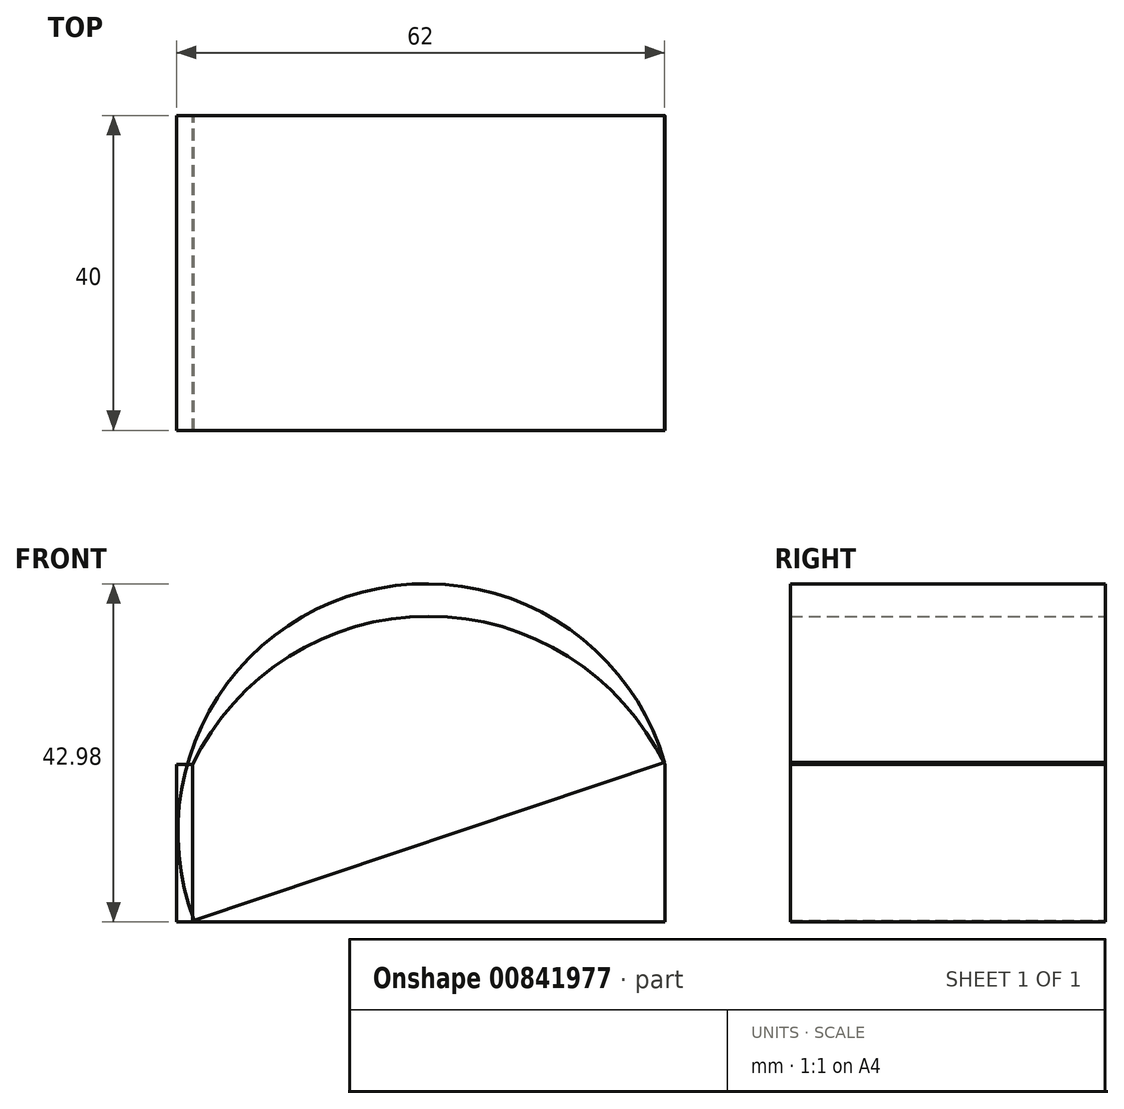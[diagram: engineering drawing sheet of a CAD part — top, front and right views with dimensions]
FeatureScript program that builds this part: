
annotation { "Feature Type Name" : "Feature", "Feature Type Description" : "" }
export const myFeature = defineFeature(function(context is Context, id is Id, definition is map)
    precondition{}
    {
        {
            var Q0;
            Q0=qCreatedBy(makeId("Front.planeOp"),FACE);
            var sketch = newSketch(context, id + "F0", { "sketchPlane" : qUnion([Q0])});
            skLineSegment(sketch, "E0.bottom", {"start": v(-32.74, -13.82) * mm, "end": v(27.26, -13.82) * mm});
            skLineSegment(sketch, "E0.top", {"start": v(-32.74, -33.82) * mm, "end": v(27.26, -33.82) * mm});
            skLineSegment(sketch, "E0.left", {"start": v(-32.74, -13.82) * mm, "end": v(-32.74, -33.82) * mm});
            skLineSegment(sketch, "E0.right", {"start": v(27.26, -13.82) * mm, "end": v(27.26, -33.82) * mm});
            skArc(sketch, "E1", {"start": v(27.26, -13.82) * mm, "mid": v(-2.74, 5.03) * mm, "end": v(-32.74, -13.82) * mm});
            skSolve(sketch);
        }
        {
            var Q0;
            Q0=makeQuery(id+"F0.imprint","IMPRINT",FACE,{"disambiguationData":[TD([[makeQuery(id+"F0.imprint","IMPRINT",EDGE,{"derivedFrom":sQuery(id+"F0.wireOp",EDGE,"E0.bottom")}),-1.0]])]});
            var Q1;
            Q1=makeQuery(id+"F0.imprint","IMPRINT",FACE,{"disambiguationData":[TD([[makeQuery(id+"F0.imprint","IMPRINT",EDGE,{"derivedFrom":sQuery(id+"F0.wireOp",EDGE,"E0.bottom")}),1.0]])]});
            extrude(context, id + "F1", {"entities" : qUnion([Q0, Q1]), "depth" : 40 * mm, "offsetDistance" : 25 * mm});
        }
        {
            var Q0;
            Q0=qCreatedBy(makeId("Front.planeOp"),FACE);
            var sketch = newSketch(context, id + "F2", { "sketchPlane" : qUnion([Q0])});
            skLineSegment(sketch, "E2", {"start": v(27.26, -13.52) * mm, "end": v(-32.54, -33.6) * mm});
            skArc(sketch, "E3", {"start": v(27.26, -13.52) * mm, "mid": v(-13.07, 7.52) * mm, "end": v(-32.54, -33.6) * mm});
            skSolve(sketch);
        }
        {
            var Q0;
            Q0=makeQuery(id+"F2.imprint","IMPRINT",FACE,{"disambiguationData":[TD([[makeQuery(id+"F2.imprint","IMPRINT",EDGE,{"derivedFrom":sQuery(id+"F2.wireOp",EDGE,"ra6rEN7m-zuiv-QKFZ-L9us-Sqd5WEpvj2RE")}),-1.0]])]});
            var Q1;
            Q1=makeQuery(id+"F2.imprint","IMPRINT",FACE,{"disambiguationData":[TD([[makeQuery(id+"F2.imprint","IMPRINT",EDGE,{"derivedFrom":sQuery(id+"F2.wireOp",EDGE,"E2")}),-1.0]])]});
            extrude(context, id + "F3", {"entities" : qUnion([Q0, Q1]), "depth" : 40 * mm, "offsetDistance" : 25 * mm});
        }
        {
            var Q0;
            Q0=makeQuery(id+"F1.opExtrude","SWEPT_FACE",FACE,{"disambiguationData":[OSD([sQuery(id+"F0.wireOp",EDGE,"E0.left")])]});
            var sketch = newSketch(context, id + "F4", { "sketchPlane" : qUnion([Q0])});
            skLineSegment(sketch, "E4.bottom", {"start": v(0, -13.82) * mm, "end": v(40, -13.82) * mm});
            skLineSegment(sketch, "E4.top", {"start": v(0, -33.82) * mm, "end": v(40, -33.82) * mm});
            skLineSegment(sketch, "E4.left", {"start": v(0, -13.82) * mm, "end": v(0, -33.82) * mm});
            skLineSegment(sketch, "E4.right", {"start": v(40, -13.82) * mm, "end": v(40, -33.82) * mm});
            skSolve(sketch);
        }
        {
            var Q0;
            Q0=makeQuery(id+"F4.imprint","IMPRINT",FACE,{"disambiguationData":[TD([[makeQuery(id+"F4.imprint","IMPRINT",EDGE,{"derivedFrom":sQuery(id+"F4.wireOp",EDGE,"E4.bottom")}),1.0]])]});
            extrude(context, id + "F5", {"entities" : qUnion([Q0]), "depth" : 2 * mm, "offsetDistance" : 25 * mm});
        }
    });
